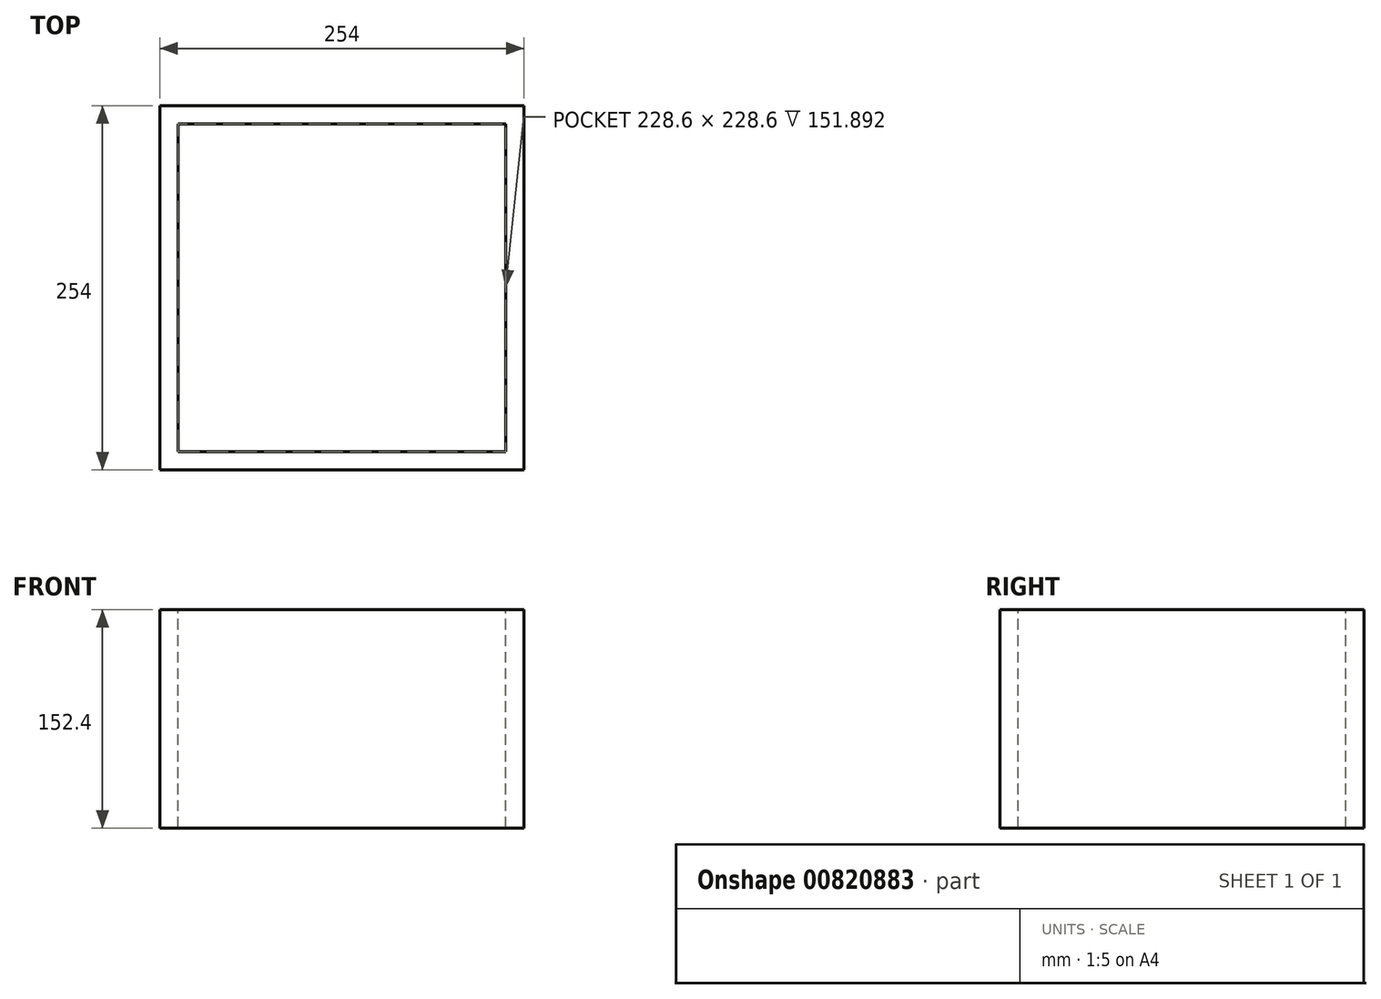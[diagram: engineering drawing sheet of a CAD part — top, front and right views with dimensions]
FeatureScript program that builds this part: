
annotation { "Feature Type Name" : "Feature", "Feature Type Description" : "" }
export const myFeature = defineFeature(function(context is Context, id is Id, definition is map)
    precondition{}
    {
        {
            var Q0;
            Q0=qCreatedBy(makeId("Top.planeOp"),FACE);
            var sketch = newSketch(context, id + "F0", { "sketchPlane" : qUnion([Q0])});
            skLineSegment(sketch, "E0", {"start": v(0, 0) * mm, "end": v(-127, 0) * mm});
            skLineSegment(sketch, "E1", {"start": v(0, 0) * mm, "end": v(127, 0) * mm});
            skLineSegment(sketch, "E2", {"start": v(-127, 0) * mm, "end": v(-127, 127) * mm});
            skLineSegment(sketch, "E3", {"start": v(127, 0) * mm, "end": v(127, 127) * mm});
            skLineSegment(sketch, "E4", {"start": v(-127, 0) * mm, "end": v(-127, -127) * mm});
            skLineSegment(sketch, "E5", {"start": v(127, 0) * mm, "end": v(127, -127) * mm});
            skLineSegment(sketch, "E6", {"start": v(-127, 127) * mm, "end": v(127, 127) * mm});
            skLineSegment(sketch, "E7", {"start": v(-127, -127) * mm, "end": v(127, -127) * mm});
            skSolve(sketch);
        }
        {
            var Q0;
            Q0=qSketchRegion(id+"F0",true);
            extrude(context, id + "F1", {"entities" : qUnion([Q0]), "depth" : 152.4 * mm, "offsetDistance" : 25.4 * mm});
        }
        {
            var Q0;
            Q0=makeQuery(id+"F1.opExtrude","CAP_FACE",FACE,{"disambiguationData":[OSD([sQuery(id+"F0.wireOp",EDGE,"E2"),sQuery(id+"F0.wireOp",EDGE,"E3"),sQuery(id+"F0.wireOp",EDGE,"E4"),sQuery(id+"F0.wireOp",EDGE,"E5"),sQuery(id+"F0.wireOp",EDGE,"E6"),sQuery(id+"F0.wireOp",EDGE,"E7")])],"isStart":false});
            var sketch = newSketch(context, id + "F2", { "sketchPlane" : qUnion([Q0])});
            skLineSegment(sketch, "E8", {"start": v(0, 0) * mm, "end": v(-114.3, 0) * mm});
            skLineSegment(sketch, "E9", {"start": v(-114.3, 0) * mm, "end": v(-114.3, 114.3) * mm});
            skLineSegment(sketch, "E10", {"start": v(0, 0) * mm, "end": v(114.3, 0) * mm});
            skLineSegment(sketch, "E11", {"start": v(114.3, 0) * mm, "end": v(114.3, 114.3) * mm});
            skLineSegment(sketch, "E12", {"start": v(-114.3, 0) * mm, "end": v(-114.3, -114.3) * mm});
            skLineSegment(sketch, "E13", {"start": v(114.3, 0) * mm, "end": v(114.3, -114.3) * mm});
            skLineSegment(sketch, "E14", {"start": v(-114.3, 114.3) * mm, "end": v(114.3, 114.3) * mm});
            skLineSegment(sketch, "E15", {"start": v(-114.3, -114.3) * mm, "end": v(114.3, -114.3) * mm});
            skSolve(sketch);
        }
        {
            var Q0;
            Q0=qSketchRegion(id+"F2",true);
            extrude(context, id + "F3", {"entities" : qUnion([Q0]), "operationType" : NewBodyOperationType.REMOVE, "oppositeDirection" : true, "depth" : 151.9 * mm, "offsetDistance" : 25.4 * mm});
        }
    });
